# Revit family: PV_Compact_PN25_DN065_(50-200kPa)_RFA_2019
name_source: partatom
category: Pipe Accessories
units: mm (PartAtom-declared; Revit-internal decimal feet)

## family parameters
Always vertical = Yes
Cut with Voids When Loaded = No
Part Type = Valve - Breaks Into
Round Connector Dimension = Use Diameter
Shared = No
Work Plane-Based = No

## types (4) — shared parameters
CAT0 = Yes
Description = Nastavitelný regulátor tlakové diference
L2D = 230 mm
L2D_Min = 30 mm  [stored 0.0984252 ft]
MC Pressure Drop Maximum Value = 0.0 Pa
MC Pressure Drop Minimum Value = 0.0 Pa
MC Use Limits From Balancing Method = No
Manufacturer = Hydronic Systems Prague s.r.o.
QmdConnectorList = 301;D;302;D
Type Comments = PŘÍRUBOVÝ; PN25; dpmax=1000kPa; -10~+120°C
URL = www.hydronic.cz
W2D = 50 mm  [stored 0.164042 ft]
magiPartTypeId = 304
magiProductFamilyId = 1af2f5f7761a4c5f850eea414834fa
zero-valued in all types: MC Throttling Maximum Value, MC Throttling Minimum Value

## per-type parameters (varying)
| type | D | DF2 | H1 | H2 | H3 | H4 | H6 | L2 | L3 | L4 | LF | LF2 | LF__ve | MC Product Code | R1 | R3 | R4 | magiProductId |
| PV Compact PN25 DN050 (50-200kPa) | 50 mm | 83 mm | 124 mm | 62 mm | 21 mm | 25 mm  [stored 0.082021 ft] | 82 mm | 115 mm  [stored 0.377297 ft] | 193 mm | 108 mm | 18 mm | 9 mm  [stored 0.0295276 ft] | -18 mm | 53-3321 DN050 PN25; nastavitelný rozsah dp=20~100kPa; Q=5,1~20,5 m3/h;  kvs=29 | 58 mm | 43 mm | 40 mm | 08a421d9482846e584fc1251b4b528 |
| PV Compact PN25 DN065 (50-200kPa) | 65 mm | 93 mm | 139 mm | 69 mm | 23 mm | 28 mm  [stored 0.0918635 ft] | 105 mm | 145 mm | 244 mm | 136 mm | 23 mm | 12 mm  [stored 0.0393701 ft] | -23 mm | 53-3324 DN065 PN25; nastavitelný rozsah dp=20~100kPa; Q=7,4~29,7 m3/h;  kvs=42 | 73 mm | 48 mm | 51 mm | 3326a2f4bd724a059fd12b24a48407 |
| PV Compact PN25 DN080 (50-200kPa) | 80 mm | 100 mm  [stored 0.328084 ft] | 150 mm | 75 mm  [stored 0.246063 ft] | 25 mm  [stored 0.082021 ft] | 30 mm  [stored 0.0984252 ft] | 141 mm | 155 mm | 260 mm | 146 mm | 25 mm  [stored 0.082021 ft] | 12 mm  [stored 0.0393701 ft] | -25 mm | 53-3327 DN080 PN25; nastavitelný rozsah dp=20~100kPa; Q=11,7~47,4 m3/h;  kvs=67 | 78 mm | 52 mm  [stored 0.170604 ft] | 54 mm | aa373f4712fe4f789034ae13a1f456 |
| PV Compact PN25 DN100 (50-200kPa) | 100 mm | 118 mm | 176 mm | 88 mm | 29 mm | 35 mm | 235 mm | 175 mm | 294 mm | 165 mm | 28 mm  [stored 0.0918635 ft] | 14 mm  [stored 0.0459318 ft] | -28 mm  [stored -0.0918635 ft] | 53-3330 DN100 PN25; nastavitelný rozsah dp=20~100kPa; Q=20,3~81,3 m3/h;  kvs=115 | 88 mm | 61 mm | 61 mm | 7d735ad2cc7a4544b6e207f0b5dfca |

note: [stored X ft] marks values corroborated as IEEE doubles in the binary element streams (Revit-internal decimal feet)

## geometry (parser evidence)
native form markers: Sweep x1
no freeform markers — native parametric forms only
